# Revit family: Sanitary_Taps-Mixers_hansgrohe_76050CHN-Finoris-Single-lever-basin-mixe_NEW
name_source: partatom
category: Plumbing Fixtures
revit_build: Autodesk Revit 2015 (Build: 20140903_1530(x64)
units: mm (PartAtom-declared; Revit-internal decimal feet)

## types (3) — shared parameters
Always visible = Yes
BIMobject category = Taps & Mixers
BIMobject category code = sanitary-taps-mixers
BIMobject main category = Sanitary
BIMobject main category code = sanitary
Brand url = http://www.hansgrohe-int.com
Design country = Germany
Edition number = 1
IFC Classification = Sanitary Terminal
Installation instructions = https://www.hansgrohe.com
Manufacturer country = Germany
Manufacturer name = hansgrohe
Material main = Chrome
Product Guid = 19c5dacf-f3bf-4548-a0d2-d5f10c91a196
Product SKU = 76050CHN
Product data url = https://bimobject.com
Product family = Finoris
Product group = Basin mixers
Product name = 76050CHN Finoris Single lever basin mixer for concealed installation wall-mounted with spout 22,5 cm
Product url = https://www.hansgrohe.com
QR code = http://bimobject.com
Technical description = https://www.hansgrohe.com

## per-type parameters (varying)
| type | Material 1 |
| 707 Matt white | Hansgrohe - Finoris - 707 Matt white |
| 677 Matt black | Hansgrohe - Finoris - 677 Matt black |
| 007 Chrome | Hansgrohe - Finoris - 007 Chrome |

## geometry (parser evidence)
native form markers: Sweep x3
no freeform markers — native parametric forms only
